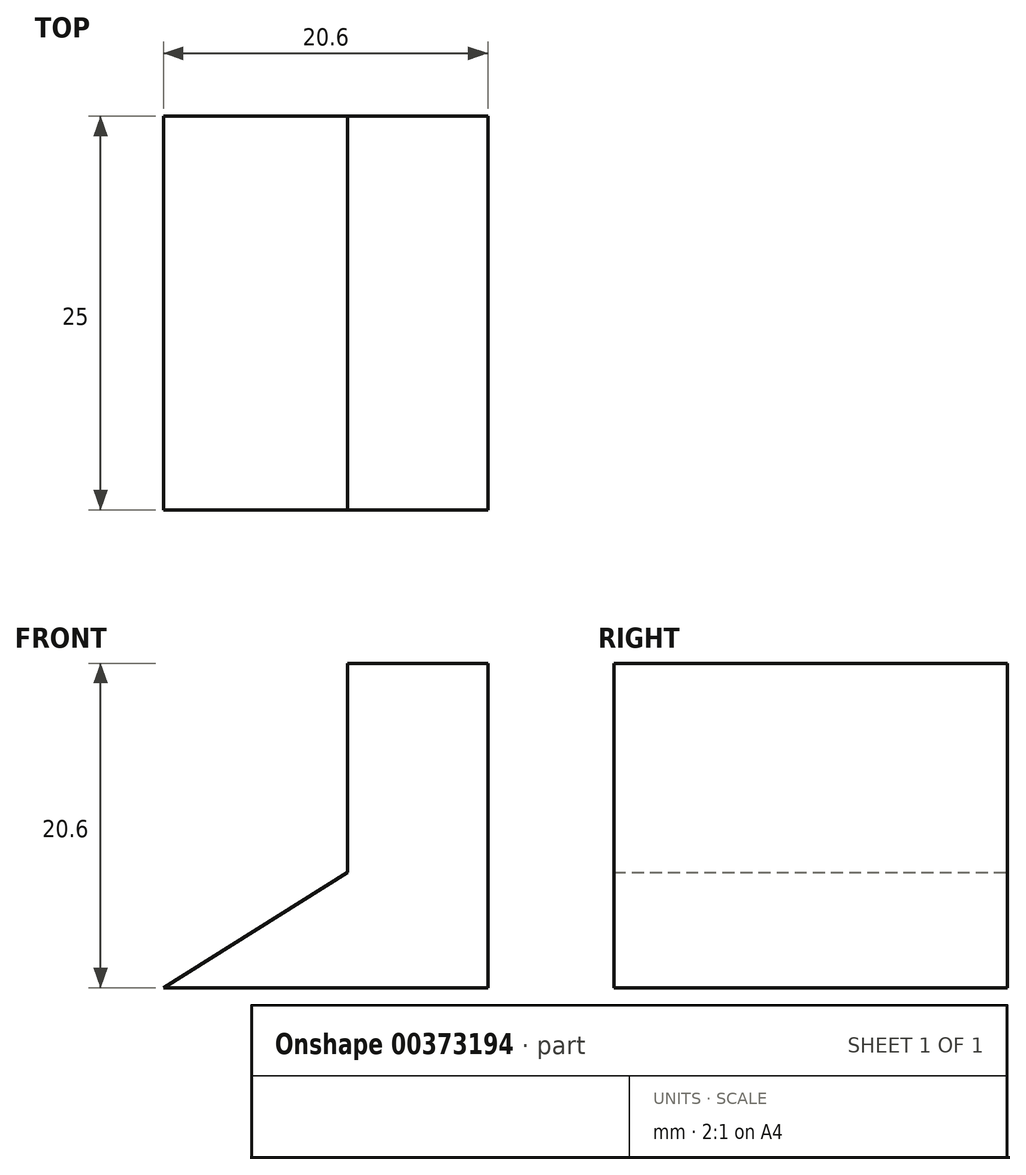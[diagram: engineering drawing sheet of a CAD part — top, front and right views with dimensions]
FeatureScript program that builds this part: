
annotation { "Feature Type Name" : "Feature", "Feature Type Description" : "" }
export const myFeature = defineFeature(function(context is Context, id is Id, definition is map)
    precondition{}
    {
        {
            var Q0;
            Q0=qCreatedBy(makeId("Front.planeOp"),FACE);
            var sketch = newSketch(context, id + "F0", { "sketchPlane" : qUnion([Q0])});
            skLineSegment(sketch, "E0", {"start": v(0, 0) * mm, "end": v(0, 20.6) * mm});
            skLineSegment(sketch, "E1", {"start": v(0, 0) * mm, "end": v(-20.6, 0) * mm});
            skLineSegment(sketch, "E2", {"start": v(-20.6, 0) * mm, "end": v(-8.93, 7.33) * mm});
            skLineSegment(sketch, "E3", {"start": v(0, 20.6) * mm, "end": v(-8.93, 20.6) * mm});
            skLineSegment(sketch, "E4", {"start": v(-8.93, 20.6) * mm, "end": v(-8.93, 7.33) * mm});
            skSolve(sketch);
        }
        {
            var Q0;
            Q0 = qSketchRegion(id + "F0", true);
            extrude(context, id + "F1", {"entities" : qUnion([Q0]), "depth" : 25 * mm});
        }
    });
